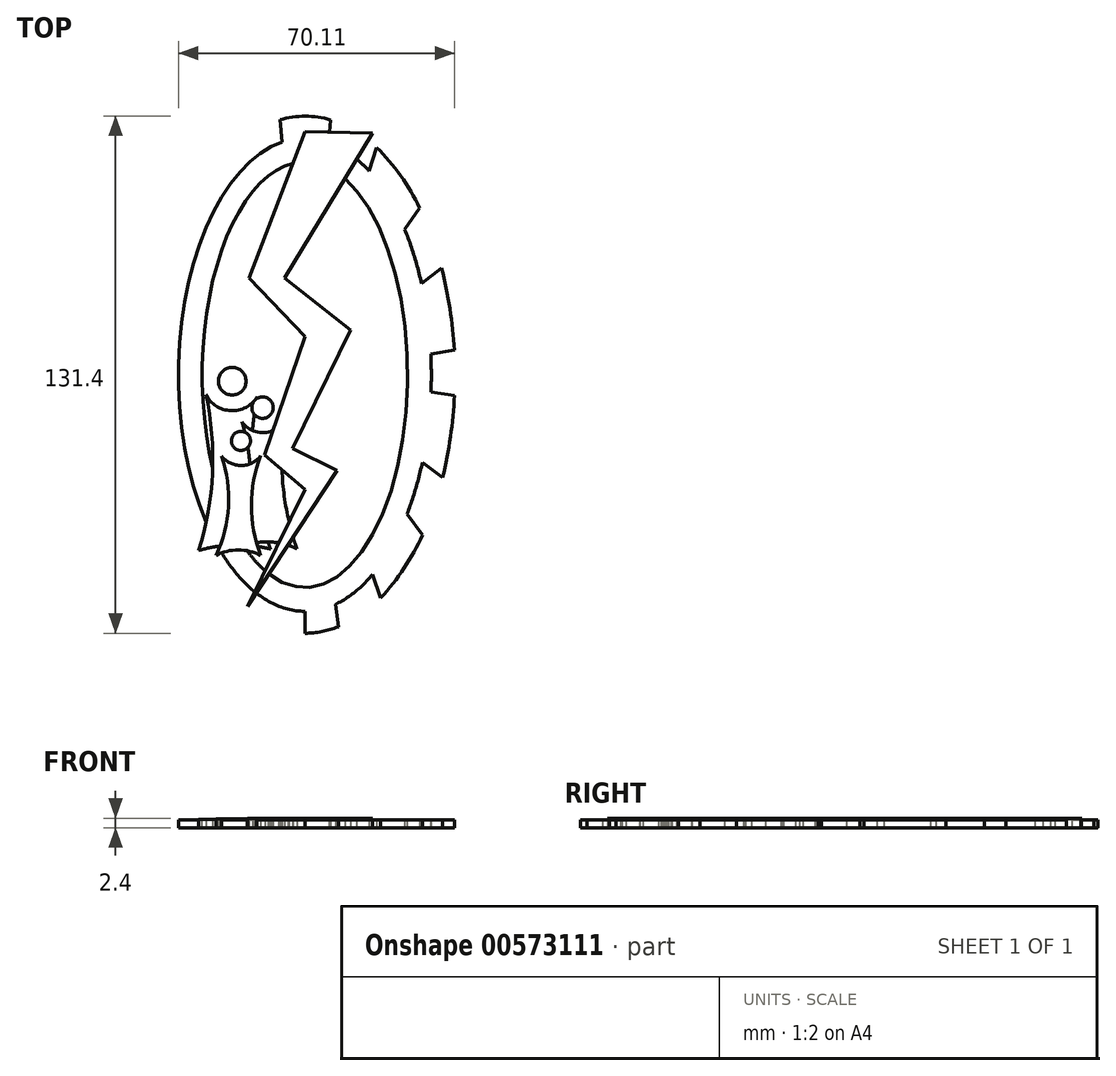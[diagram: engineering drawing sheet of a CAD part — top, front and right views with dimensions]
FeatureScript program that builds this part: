
annotation { "Feature Type Name" : "Feature", "Feature Type Description" : "" }
export const myFeature = defineFeature(function(context is Context, id is Id, definition is map)
    precondition{}
    {
        {
            var Q0;
            Q0=qCreatedBy(makeId("Top.planeOp"),FACE);
            var sketch = newSketch(context, id + "F0", { "sketchPlane" : qUnion([Q0])});
            skEllipse(sketch, "E0", {"center": v(0, 0) * mm, "majorRadius": 65.7 * mm, "minorRadius": 38.12 * mm, "majorAxis": v(0, 1), "construction": true});
            skEllipse(sketch, "E1", {"center": v(0, 0) * mm, "majorRadius": 60.1 * mm, "minorRadius": 32.1 * mm, "majorAxis": v(0, 1)});
            skEllipse(sketch, "E2", {"center": v(0, 0) * mm, "majorRadius": 54.05 * mm, "minorRadius": 26.1 * mm, "majorAxis": v(0, 1)});
            skLineSegment(sketch, "E3", {"start": v(0, 0) * mm, "end": v(0, 77.35) * mm, "construction": true});
            skPoint(sketch, "E3.endSnap0", {"position": v(0, 65.7) * mm});
            skLineSegment(sketch, "E4", {"start": v(0, 0) * mm, "end": v(7.92, 78.28) * mm, "construction": true});
            skLineSegment(sketch, "E5", {"start": v(0, 0) * mm, "end": v(16.3, 79.2) * mm, "construction": true});
            skLineSegment(sketch, "E6", {"start": v(0, 0) * mm, "end": v(-7.92, 80.6) * mm, "construction": true});
            skLineSegment(sketch, "E7.MirrorCS", {"start": v(0, 0) * mm, "end": v(23.64, 75.04) * mm, "construction": true});
            skLineSegment(sketch, "E8.MirrorCS", {"start": v(0, 0) * mm, "end": v(30.55, 71.05) * mm, "construction": true});
            skLineSegment(sketch, "E9.MirrorCS", {"start": v(0, 0) * mm, "end": v(39.12, 70.92) * mm, "construction": true});
            skLineSegment(sketch, "E10.MirrorCS", {"start": v(0, 0) * mm, "end": v(43.8, 63.75) * mm, "construction": true});
            skLineSegment(sketch, "E11.MirrorCS", {"start": v(0, 0) * mm, "end": v(50.86, 60.03) * mm, "construction": true});
            skLineSegment(sketch, "E12.MirrorCS", {"start": v(0, 0) * mm, "end": v(58.3, 56.05) * mm, "construction": true});
            skLineSegment(sketch, "E13.MirrorCS", {"start": v(0, 0) * mm, "end": v(61.98, 48.46) * mm, "construction": true});
            skLineSegment(sketch, "E14.MirrorCS", {"start": v(0, 0) * mm, "end": v(65.42, 41.26) * mm, "construction": true});
            skLineSegment(sketch, "E15.MirrorCS", {"start": v(0, 0) * mm, "end": v(72.4, 36.3) * mm, "construction": true});
            skLineSegment(sketch, "E16.MirrorCS", {"start": v(0, 0) * mm, "end": v(72.2, 27.74) * mm, "construction": true});
            skLineSegment(sketch, "E17.MirrorCS", {"start": v(0, 0) * mm, "end": v(75.91, 20.68) * mm, "construction": true});
            skLineSegment(sketch, "E18.MirrorCS", {"start": v(0, 0) * mm, "end": v(79.79, 13.18) * mm, "construction": true});
            skLineSegment(sketch, "E19.MirrorCS", {"start": v(0, 0) * mm, "end": v(78.53, 4.84) * mm, "construction": true});
            skLineSegment(sketch, "E20.MirrorCS", {"start": v(0, 0) * mm, "end": v(77.29, -3.04) * mm, "construction": true});
            skLineSegment(sketch, "E21.MirrorCS", {"start": v(0, 0) * mm, "end": v(80.23, -11.08) * mm, "construction": true});
            skLineSegment(sketch, "E22.MirrorCS", {"start": v(0, 0) * mm, "end": v(75.22, -18.02) * mm, "construction": true});
            skLineSegment(sketch, "E23.MirrorCS", {"start": v(0, 0) * mm, "end": v(74.28, -25.94) * mm, "construction": true});
            skLineSegment(sketch, "E24.MirrorCS", {"start": v(0, 0) * mm, "end": v(73.23, -34.32) * mm, "construction": true});
            skLineSegment(sketch, "E25.MirrorCS", {"start": v(0, 0) * mm, "end": v(67.46, -40.48) * mm, "construction": true});
            skLineSegment(sketch, "E26.MirrorCS", {"start": v(0, 0) * mm, "end": v(61.98, -46.27) * mm, "construction": true});
            skLineSegment(sketch, "E27.MirrorCS", {"start": v(0, 0) * mm, "end": v(59.85, -54.57) * mm, "construction": true});
            skLineSegment(sketch, "E28.MirrorCS", {"start": v(0, 0) * mm, "end": v(51.79, -57.45) * mm, "construction": true});
            skLineSegment(sketch, "E29.MirrorCS", {"start": v(0, 0) * mm, "end": v(46.53, -63.44) * mm, "construction": true});
            skLineSegment(sketch, "E30.MirrorCS", {"start": v(0, 0) * mm, "end": v(40.92, -69.75) * mm, "construction": true});
            skLineSegment(sketch, "E31.MirrorCS", {"start": v(0, 0) * mm, "end": v(32.68, -71.57) * mm, "construction": true});
            skLineSegment(sketch, "E32.MirrorCS", {"start": v(0, 0) * mm, "end": v(24.88, -73.23) * mm, "construction": true});
            skLineSegment(sketch, "E33.MirrorCS", {"start": v(0, 0) * mm, "end": v(18.43, -78.87) * mm, "construction": true});
            skLineSegment(sketch, "E34.MirrorCS", {"start": v(0, 0) * mm, "end": v(10.15, -76.68) * mm, "construction": true});
            skLineSegment(sketch, "E35.MirrorCS", {"start": v(0, 0) * mm, "end": v(2.42, -78.64) * mm, "construction": true});
            skLineSegment(sketch, "E36.MirrorCS", {"start": v(0, 0) * mm, "end": v(-5.77, -80.66) * mm, "construction": true});
            skLineSegment(sketch, "E37", {"start": v(-5.8, 59.11) * mm, "end": v(-6.37, 64.77) * mm});
            skLineSegment(sketch, "E38", {"start": v(5.98, 59.06) * mm, "end": v(6.55, 64.72) * mm});
            skArc(sketch, "E39", {"start": v(6.55, 64.72) * mm, "mid": v(0.1, 65.7) * mm, "end": v(-6.37, 64.77) * mm});
            skLineSegment(sketch, "E40", {"start": v(18.2, 57.73) * mm, "end": v(16.31, 51.77) * mm});
            skLineSegment(sketch, "E41", {"start": v(29.12, 42.39) * mm, "end": v(25.35, 36.9) * mm});
            skArc(sketch, "E42", {"start": v(29.12, 42.39) * mm, "mid": v(24.34, 50.55) * mm, "end": v(18.2, 57.73) * mm});
            skLineSegment(sketch, "E43", {"start": v(31.98, 5.29) * mm, "end": v(37.94, 6.27) * mm});
            skLineSegment(sketch, "E44", {"start": v(29.63, 23.16) * mm, "end": v(34.71, 27.14) * mm});
            skArc(sketch, "E45", {"start": v(37.94, 6.27) * mm, "mid": v(36.84, 16.78) * mm, "end": v(34.71, 27.14) * mm});
            skLineSegment(sketch, "E46", {"start": v(32.02, -4.42) * mm, "end": v(38, -5.25) * mm});
            skLineSegment(sketch, "E47", {"start": v(29.82, -22.26) * mm, "end": v(34.98, -26.11) * mm});
            skArc(sketch, "E48", {"start": v(34.98, -26.11) * mm, "mid": v(36.97, -15.75) * mm, "end": v(38, -5.25) * mm});
            skLineSegment(sketch, "E49", {"start": v(25.95, -35.39) * mm, "end": v(29.9, -40.76) * mm});
            skLineSegment(sketch, "E50", {"start": v(17.23, -50.72) * mm, "end": v(19.26, -56.7) * mm});
            skArc(sketch, "E51", {"start": v(19.26, -56.7) * mm, "mid": v(25.2, -49.15) * mm, "end": v(29.9, -40.76) * mm});
            skLineSegment(sketch, "E52", {"start": v(0, 0) * mm, "end": v(0, -83.25) * mm, "construction": true});
            skLineSegment(sketch, "E53", {"start": v(0, -60.1) * mm, "end": v(0, -65.7) * mm});
            skLineSegment(sketch, "E54", {"start": v(7.72, -58.34) * mm, "end": v(8.48, -64.05) * mm});
            skArc(sketch, "E55", {"start": v(0, -65.7) * mm, "mid": v(4.31, -65.26) * mm, "end": v(8.48, -64.05) * mm});
            skSolve(sketch);
        }
        {
            var Q0;
            Q0=makeQuery(id+"F0.imprint","IMPRINT",FACE,{"disambiguationData":[TD([[makeQuery(id+"F0.imprint","IMPRINT",EDGE,{"derivedFrom":sQuery(id+"F0.wireOp",EDGE,"E2")}),-1.0]])]});
            var Q1;
            {var subQ0=sQuery(id+"F0.wireOp",EDGE,"E37");Q1=makeQuery(id+"F0.imprint","IMPRINT",FACE,{"disambiguationData":[TD([[makeQuery(id+"F0.imprint","IMPRINT",EDGE,{"derivedFrom":subQ0}),-1.0]])]});}
            var Q2;
            {var subQ0=sQuery(id+"F0.wireOp",EDGE,"E40");Q2=makeQuery(id+"F0.imprint","IMPRINT",FACE,{"disambiguationData":[TD([[makeQuery(id+"F0.imprint","IMPRINT",EDGE,{"derivedFrom":subQ0}),1.0]])]});}
            var Q3;
            {var subQ0=sQuery(id+"F0.wireOp",EDGE,"E43");Q3=makeQuery(id+"F0.imprint","IMPRINT",FACE,{"disambiguationData":[TD([[makeQuery(id+"F0.imprint","IMPRINT",EDGE,{"derivedFrom":subQ0}),1.0]])]});}
            var Q4;
            {var subQ0=sQuery(id+"F0.wireOp",EDGE,"E46");Q4=makeQuery(id+"F0.imprint","IMPRINT",FACE,{"disambiguationData":[TD([[makeQuery(id+"F0.imprint","IMPRINT",EDGE,{"derivedFrom":subQ0}),-1.0]])]});}
            var Q5;
            {var subQ0=sQuery(id+"F0.wireOp",EDGE,"E49");Q5=makeQuery(id+"F0.imprint","IMPRINT",FACE,{"disambiguationData":[TD([[makeQuery(id+"F0.imprint","IMPRINT",EDGE,{"derivedFrom":subQ0}),-1.0]])]});}
            var Q6;
            {var subQ0=sQuery(id+"F0.wireOp",EDGE,"E53");Q6=makeQuery(id+"F0.imprint","IMPRINT",FACE,{"disambiguationData":[TD([[makeQuery(id+"F0.imprint","IMPRINT",EDGE,{"derivedFrom":subQ0}),1.0]])]});}
            extrude(context, id + "F1", {"entities" : qUnion([Q0, Q1, Q2, Q3, Q4, Q5, Q6]), "depth" : 2 * mm, "offsetDistance" : 25.4 * mm});
        }
        {
            var Q0;
            Q0=qCreatedBy(makeId("Top.planeOp"),FACE);
            var sketch = newSketch(context, id + "F2", { "sketchPlane" : qUnion([Q0])});
            skLineSegment(sketch, "E56", {"start": v(0, 61.74) * mm, "end": v(-14.2, 24.55) * mm});
            skLineSegment(sketch, "E57", {"start": v(-14.2, 24.55) * mm, "end": v(0, 9.67) * mm});
            skLineSegment(sketch, "E58", {"start": v(0, 9.67) * mm, "end": v(-10.32, -20.4) * mm});
            skLineSegment(sketch, "E59", {"start": v(-10.32, -20.4) * mm, "end": v(0, -29.13) * mm});
            skLineSegment(sketch, "E60", {"start": v(0, -29.13) * mm, "end": v(-14.52, -58.89) * mm});
            skLineSegment(sketch, "E61", {"start": v(-14.52, -58.89) * mm, "end": v(8.11, -24.28) * mm});
            skLineSegment(sketch, "E62", {"start": v(8.11, -24.28) * mm, "end": v(-3.19, -18.77) * mm});
            skLineSegment(sketch, "E63", {"start": v(-3.19, -18.77) * mm, "end": v(11.53, 11.38) * mm});
            skLineSegment(sketch, "E64", {"start": v(11.53, 11.38) * mm, "end": v(-5.14, 24.55) * mm});
            skLineSegment(sketch, "E65", {"start": v(-5.14, 24.55) * mm, "end": v(17.17, 61.42) * mm});
            skLineSegment(sketch, "E66", {"start": v(17.17, 61.42) * mm, "end": v(0, 61.74) * mm});
            skSolve(sketch);
        }
        {
            var Q0;
            Q0=makeQuery(id+"F2.imprint","IMPRINT",FACE,{"disambiguationData":[TD([[makeQuery(id+"F2.imprint","IMPRINT",EDGE,{"derivedFrom":sQuery(id+"F2.wireOp",EDGE,"E56")}),1.0]])]});
            extrude(context, id + "F3", {"entities" : qUnion([Q0]), "operationType" : NewBodyOperationType.ADD, "depth" : 2.4 * mm, "offsetDistance" : 25 * mm});
        }
        {
            var Q0;
            Q0=qCreatedBy(makeId("Top.planeOp"),FACE);
            var sketch = newSketch(context, id + "F4", { "sketchPlane" : qUnion([Q0])});
            skArc(sketch, "E67", {"start": v(-25.16, -5.03) * mm, "mid": v(-18.82, -9.13) * mm, "end": v(-12.14, -5.63) * mm});
            skArc(sketch, "E68", {"start": v(-27.01, -44.65) * mm, "mid": v(-23.49, -24.96) * mm, "end": v(-25.16, -5.03) * mm});
            skArc(sketch, "E69", {"start": v(-12.14, -5.63) * mm, "mid": v(-13.23, -25.2) * mm, "end": v(-8.72, -44.28) * mm});
            skArc(sketch, "E70", {"start": v(-8.72, -44.28) * mm, "mid": v(-17.89, -43.29) * mm, "end": v(-27.01, -44.65) * mm});
            skCircle(sketch, "E71", {"center": v(-18.48, -1.65) * mm, "radius": 3.52 * mm});
            skSolve(sketch);
        }
        {
            var Q0;
            Q0=makeQuery(id+"F4.imprint","IMPRINT",FACE,{"disambiguationData":[TD([[makeQuery(id+"F4.imprint","IMPRINT",EDGE,{"derivedFrom":sQuery(id+"F4.wireOp",EDGE,"E67")}),-1.0]])]});
            var Q1;
            Q1=makeQuery(id+"F4.imprint","IMPRINT",FACE,{"disambiguationData":[TD([[makeQuery(id+"F4.imprint","IMPRINT",EDGE,{"derivedFrom":sQuery(id+"F4.wireOp",EDGE,"E71")}),1.0]])]});
            extrude(context, id + "F5", {"entities" : qUnion([Q0, Q1]), "operationType" : NewBodyOperationType.ADD, "depth" : 2.1 * mm, "offsetDistance" : 25 * mm});
        }
        {
            var Q0;
            Q0=qCreatedBy(makeId("Top.planeOp"),FACE);
            var sketch = newSketch(context, id + "F6", { "sketchPlane" : qUnion([Q0])});
            skArc(sketch, "E72", {"start": v(-16.02, -11.95) * mm, "mid": v(-10.33, -14.72) * mm, "end": v(-5.07, -11.2) * mm});
            skArc(sketch, "E73", {"start": v(-17.61, -44.32) * mm, "mid": v(-13.96, -28.28) * mm, "end": v(-16.02, -11.95) * mm});
            skArc(sketch, "E74", {"start": v(-5.07, -11.2) * mm, "mid": v(-5.59, -27.9) * mm, "end": v(-2.03, -44.23) * mm});
            skArc(sketch, "E75", {"start": v(-2.03, -44.23) * mm, "mid": v(-9.83, -42.47) * mm, "end": v(-17.61, -44.32) * mm});
            skCircle(sketch, "E76", {"center": v(-10.76, -8.37) * mm, "radius": 2.72 * mm});
            skSolve(sketch);
        }
        {
            var Q0;
            Q0 = qSketchRegion(id + "F6", true);
            extrude(context, id + "F7", {"entities" : qUnion([Q0]), "operationType" : NewBodyOperationType.ADD, "depth" : 2.2 * mm, "offsetDistance" : 25 * mm});
        }
        {
            var Q0;
            Q0=qCreatedBy(makeId("Top.planeOp"),FACE);
            var sketch = newSketch(context, id + "F8", { "sketchPlane" : qUnion([Q0])});
            skArc(sketch, "E77", {"start": v(-21.14, -20.7) * mm, "mid": v(-16.15, -23.07) * mm, "end": v(-11.22, -20.55) * mm});
            skArc(sketch, "E78", {"start": v(-22.62, -45.87) * mm, "mid": v(-19.4, -33.43) * mm, "end": v(-21.14, -20.7) * mm});
            skArc(sketch, "E79", {"start": v(-11.22, -20.55) * mm, "mid": v(-13.6, -33.2) * mm, "end": v(-11.22, -45.87) * mm});
            skArc(sketch, "E80", {"start": v(-11.22, -45.87) * mm, "mid": v(-16.92, -44.5) * mm, "end": v(-22.62, -45.87) * mm});
            skCircle(sketch, "E81", {"center": v(-16.24, -16.82) * mm, "radius": 2.43 * mm});
            skSolve(sketch);
        }
        {
            var Q0;
            Q0 = qSketchRegion(id + "F8", true);
            extrude(context, id + "F9", {"entities" : qUnion([Q0]), "operationType" : NewBodyOperationType.ADD, "depth" : 2.3 * mm, "offsetDistance" : 25 * mm});
        }
    });
